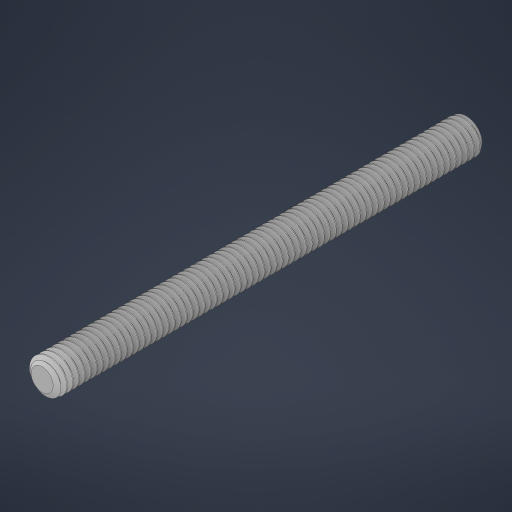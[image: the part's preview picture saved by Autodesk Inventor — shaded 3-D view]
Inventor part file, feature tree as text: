
AUTODESK INVENTOR PART (.ipt)
format: ipt  version: 2023 (Build 270158000, 158)  size: 1,856,512 bytes
history: native  units: in
note: dims shown in document units (in); Inventor stores cm internally (conversion verified against a paired STEP export)
features: mirror x1
ambient origin geometry x8: Origin, YZ Plane, XZ Plane, XY Plane, X Axis, Y Axis, Z Axis, Center Point
bodies: Solid1 (feature_tree)
feature tree (1):
  mirror  "Mirror1"
